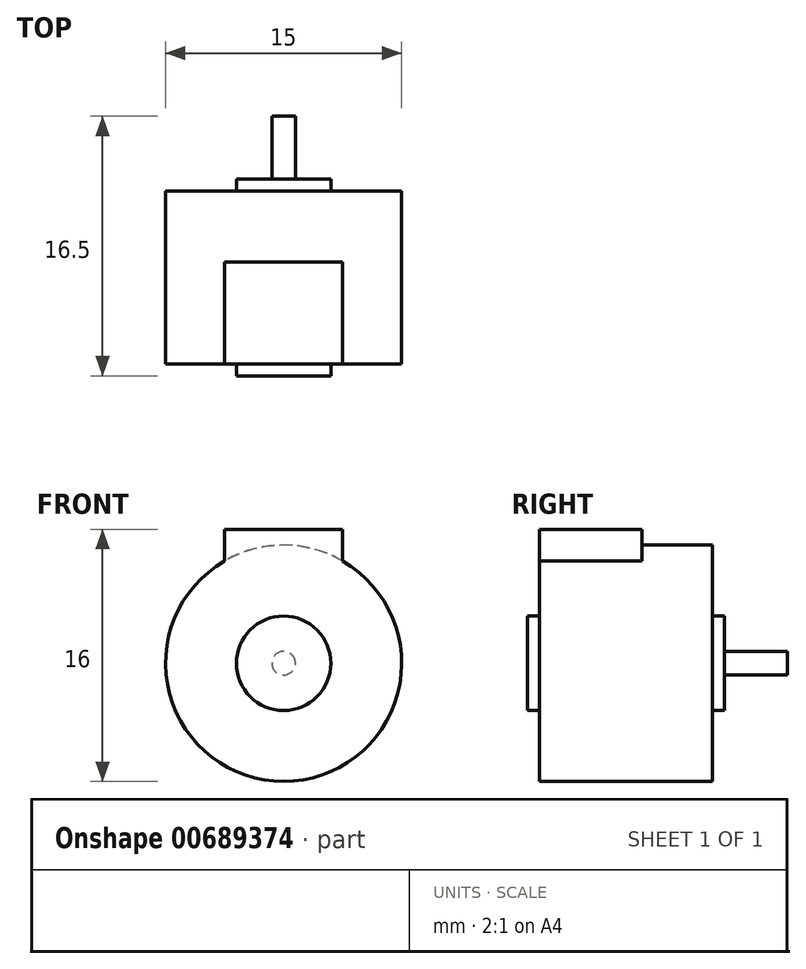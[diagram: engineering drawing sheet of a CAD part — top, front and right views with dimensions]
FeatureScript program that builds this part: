
annotation { "Feature Type Name" : "Feature", "Feature Type Description" : "" }
export const myFeature = defineFeature(function(context is Context, id is Id, definition is map)
    precondition{}
    {
        {
            var Q0;
            Q0=qCreatedBy(makeId("Front.planeOp"),FACE);
            var sketch = newSketch(context, id + "F0", { "sketchPlane" : qUnion([Q0])});
            skArc(sketch, "E0", {"start": v(-3.75, 6.5) * mm, "mid": v(0, -7.5) * mm, "end": v(3.75, 6.5) * mm});
            skLineSegment(sketch, "E1", {"start": v(-3.75, 8.5) * mm, "end": v(-3.75, 6.5) * mm});
            skLineSegment(sketch, "E2", {"start": v(-3.75, 8.5) * mm, "end": v(3.75, 8.5) * mm});
            skLineSegment(sketch, "E3", {"start": v(3.75, 8.5) * mm, "end": v(3.75, 6.5) * mm});
            skPoint(sketch, "E4.orphan", {"position": v(-3.75, 0) * mm});
            skPoint(sketch, "E5.orphan", {"position": v(3.75, 0) * mm});
            skSolve(sketch);
        }
        {
            var Q0;
            Q0=qSketchRegion(id+"F0",true);
            extrude(context, id + "F1", {"entities" : qUnion([Q0]), "depth" : 6.5 * mm});
        }
        {
            var Q0;
            Q0=makeQuery(id+"F1.opExtrude","CAP_FACE",FACE,{"disambiguationData":[OSD([sQuery(id+"F0.wireOp",EDGE,"E0"),sQuery(id+"F0.wireOp",EDGE,"E1"),sQuery(id+"F0.wireOp",EDGE,"E2"),sQuery(id+"F0.wireOp",EDGE,"E3")])],"isStart":false});
            var sketch = newSketch(context, id + "F2", { "sketchPlane" : qUnion([Q0])});
            skCircle(sketch, "E6", {"center": v(0, 0) * mm, "radius": 3 * mm});
            skSolve(sketch);
        }
        {
            var Q0;
            Q0=qSketchRegion(id+"F2",true);
            extrude(context, id + "F3", {"entities" : qUnion([Q0]), "operationType" : NewBodyOperationType.ADD, "depth" : .75 * mm, "hasSecondDirection" : true, "secondDirectionOppositeDirection" : true, "secondDirectionDepth" : 11.75 * mm});
        }
        {
            var Q0;
            Q0=makeQuery(id+"F1.opExtrude","CAP_FACE",FACE,{"disambiguationData":[OSD([sQuery(id+"F0.wireOp",EDGE,"E0"),sQuery(id+"F0.wireOp",EDGE,"E1"),sQuery(id+"F0.wireOp",EDGE,"E2"),sQuery(id+"F0.wireOp",EDGE,"E3")])],"isStart":true});
            var sketch = newSketch(context, id + "F4", { "sketchPlane" : qUnion([Q0])});
            skCircle(sketch, "E7", {"center": v(0, 0) * mm, "radius": 7.5 * mm});
            skSolve(sketch);
        }
        {
            var Q0;
            Q0=qSketchRegion(id+"F4",true);
            var Q1;
            Q1=qSketchRegion(id+"F2",true);
            extrude(context, id + "F5", {"entities" : qUnion([Q0, Q1]), "operationType" : NewBodyOperationType.ADD, "depth" : 4.5 * mm});
        }
        {
            var Q0;
            Q0=makeQuery(id+"F3.opExtrude","CAP_FACE",FACE,{"disambiguationData":[OSD([sQuery(id+"F2.wireOp",EDGE,"E6")])],"isStart":true});
            var sketch = newSketch(context, id + "F6", { "sketchPlane" : qUnion([Q0])});
            skCircle(sketch, "E8", {"center": v(0, 0) * mm, "radius": 0.75 * mm});
            skSolve(sketch);
        }
        {
            var Q0;
            Q0=qSketchRegion(id+"F6",true);
            extrude(context, id + "F7", {"entities" : qUnion([Q0]), "operationType" : NewBodyOperationType.ADD, "depth" : 4 * mm});
        }
    });
